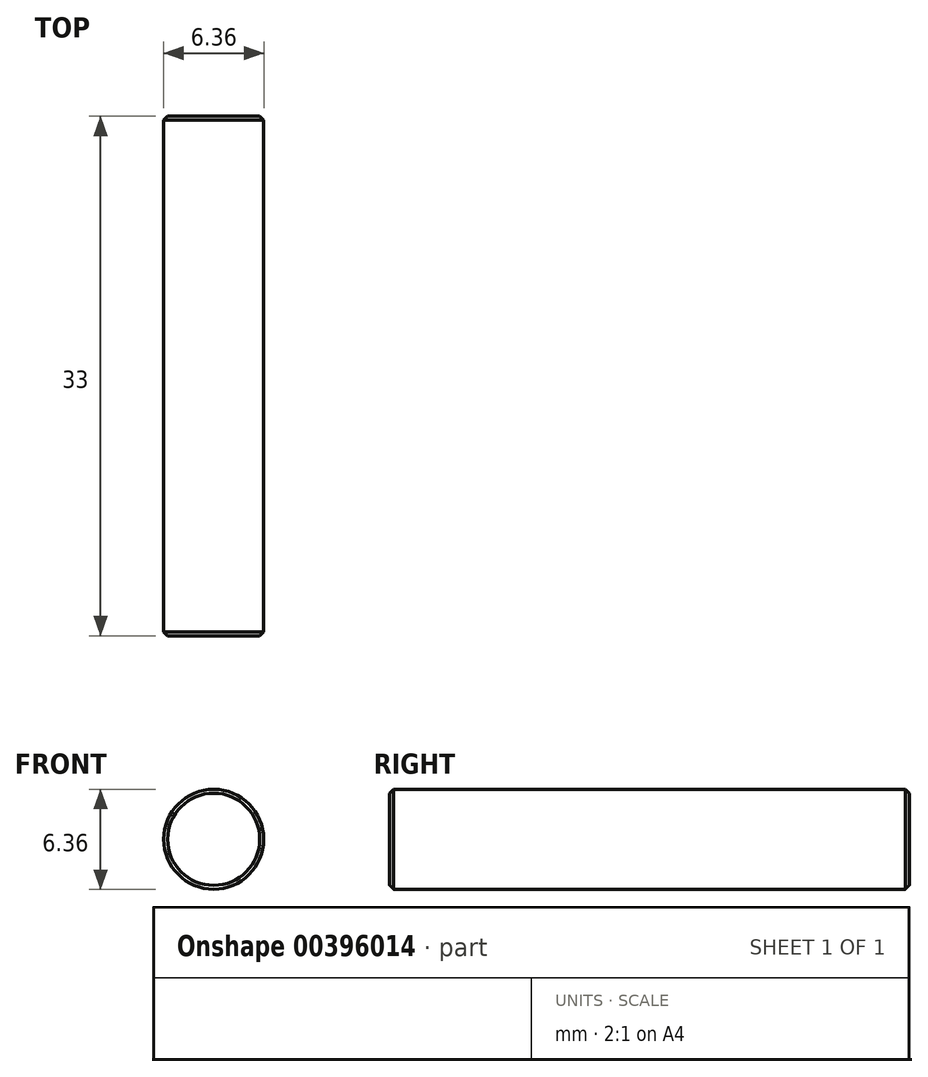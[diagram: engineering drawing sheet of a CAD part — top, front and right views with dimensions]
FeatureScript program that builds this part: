
annotation { "Feature Type Name" : "Feature", "Feature Type Description" : "" }
export const myFeature = defineFeature(function(context is Context, id is Id, definition is map)
    precondition{}
    {
        {
            var Q0;
            Q0=qCreatedBy(makeId("Front.planeOp"),FACE);
            var sketch = newSketch(context, id + "F0", { "sketchPlane" : qUnion([Q0])});
            skCircle(sketch, "E0", {"center": v(0, 0) * mm, "radius": 3.18 * mm});
            skSolve(sketch);
        }
        {
            var Q0;
            Q0 = qSketchRegion(id + "F0", true);
            extrude(context, id + "F1", {"entities" : qUnion([Q0]), "depth" : 33 * mm, "offsetDistance" : 25 * mm});
        }
        {
            var Q0;
            Q0=makeQuery(id+"F1.opExtrude","CAP_EDGE",EDGE,{"disambiguationData":[OSD([sQuery(id+"F0.wireOp",EDGE,"E0")])],"isStart":false});
            var Q1;
            Q1=makeQuery(id+"F1.opExtrude","CAP_EDGE",EDGE,{"disambiguationData":[OSD([sQuery(id+"F0.wireOp",EDGE,"E0")])],"isStart":true});
            chamfer(context, id + "F2", {"entities" : qUnion([Q0, Q1]), "width" : 0.25 * mm, "tangentPropagation" : true});
        }
    });
